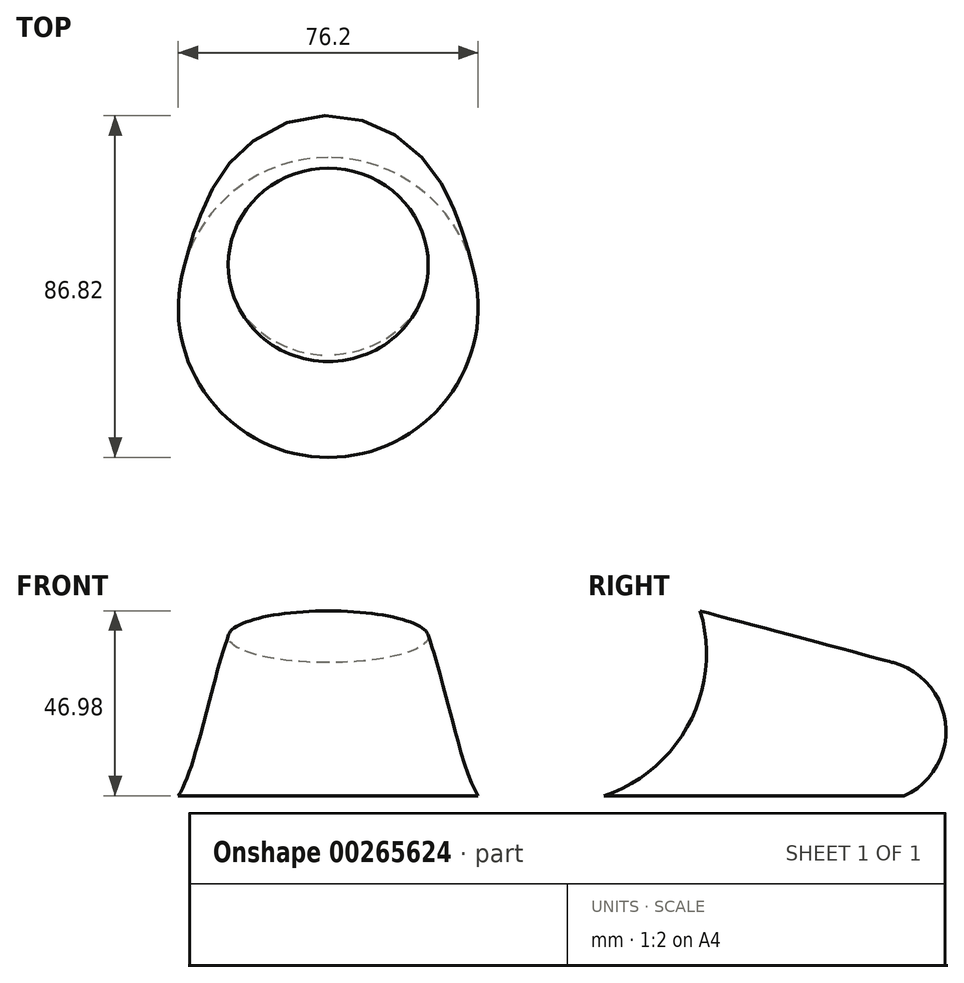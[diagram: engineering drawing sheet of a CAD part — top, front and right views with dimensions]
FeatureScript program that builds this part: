
annotation { "Feature Type Name" : "Feature", "Feature Type Description" : "" }
export const myFeature = defineFeature(function(context is Context, id is Id, definition is map)
    precondition{}
    {
        {
            var Q0;
            Q0=qCreatedBy(makeId("Top.planeOp"),FACE);
            var sketch = newSketch(context, id + "F0", { "sketchPlane" : qUnion([Q0])});
            skLineSegment(sketch, "E0.bottom", {"start": v(-63.5, 63.5) * mm, "end": v(63.5, 63.5) * mm});
            skLineSegment(sketch, "E0.top", {"start": v(-63.5, -63.5) * mm, "end": v(63.5, -63.5) * mm});
            skLineSegment(sketch, "E0.left", {"start": v(-63.5, 63.5) * mm, "end": v(-63.5, -63.5) * mm});
            skLineSegment(sketch, "E0.right", {"start": v(63.5, 63.5) * mm, "end": v(63.5, -63.5) * mm});
            skPoint(sketch, "E0.middle", {"position": v(0, 0) * mm});
            skCircle(sketch, "E1", {"center": v(0, 0) * mm, "radius": 38.1 * mm});
            skSolve(sketch);
        }
        {
            var Q0;
            Q0=sQuery(id+"F0.wireOp",EDGE,"E0.bottom");
            cPlane(context, id + "F1", {"entities" : qUnion([Q0]), "cplaneType" : CPlaneType.LINE_ANGLE, "offset" : 25.4 * mm, "angle" : 75 * degree, "width" : 152.4 * mm, "height" : 152.4 * mm});
        }
        {
            var Q0;
            Q0=qCreatedBy(id+"F1.planeOp",FACE);
            cPlane(context, id + "F2", {"entities" : qUnion([Q0]), "cplaneType" : CPlaneType.OFFSET, "offset" : 25.4 * mm, "width" : 152.4 * mm, "height" : 152.4 * mm});
        }
        {
            var Q0;
            Q0=qCreatedBy(id+"F2.planeOp",FACE);
            var sketch = newSketch(context, id + "F3", { "sketchPlane" : qUnion([Q0])});
            skCircle(sketch, "E2", {"center": v(0, 0) * mm, "radius": 25.4 * mm});
            skSolve(sketch);
        }
        {
            var Q0;
            Q0=qCreatedBy(makeId("Right.planeOp"),FACE);
            var sketch = newSketch(context, id + "F4", { "sketchPlane" : qUnion([Q0])});
            skLineSegment(sketch, "E3.0", {"start": v(-38.1, 0) * mm, "end": v(38.1, 0) * mm});
            skLineSegment(sketch, "E4.0", {"start": v(-13.7, 46.98) * mm, "end": v(35.36, 33.84) * mm});
            skArc(sketch, "E5", {"start": v(35.36, 33.84) * mm, "mid": v(48.66, 17.88) * mm, "end": v(38.1, 0) * mm});
            skArc(sketch, "E6", {"start": v(-38.1, 0) * mm, "mid": v(-16.41, 18.56) * mm, "end": v(-13.7, 46.98) * mm});
            skSolve(sketch);
        }
        {
            var Q0;
            Q0=makeQuery(id+"F0.imprint","IMPRINT",FACE,{"disambiguationData":[TD([[makeQuery(id+"F0.imprint","IMPRINT",EDGE,{"derivedFrom":sQuery(id+"F0.wireOp",EDGE,"E1")}),1.0]])]});
            var Q1;
            Q1=makeQuery(id+"F3.imprint","IMPRINT",FACE,{"disambiguationData":[TD([[makeQuery(id+"F3.imprint","IMPRINT",EDGE,{"derivedFrom":sQuery(id+"F3.wireOp",EDGE,"E2")}),1.0]])]});
            var Q2;
            Q2=sQuery(id+"F4.wireOp",EDGE,"E6");
            var Q3;
            Q3=sQuery(id+"F4.wireOp",EDGE,"E5");
            loft(context, id + "F5", {"addGuides" : true, "sheetProfilesArray" : [{ "sheetProfileEntities" : qUnion([Q0]) }, { "sheetProfileEntities" : qUnion([Q1]) }], "guidesArray" : [{ "guideEntities" : qUnion([Q2]), "guideDerivativeType" : LoftGuideDerivativeType.DEFAULT, "guideDerivativeMagnitude" : 1 }, { "guideEntities" : qUnion([Q3]), "guideDerivativeType" : LoftGuideDerivativeType.DEFAULT, "guideDerivativeMagnitude" : 1 }]});
        }
    });
